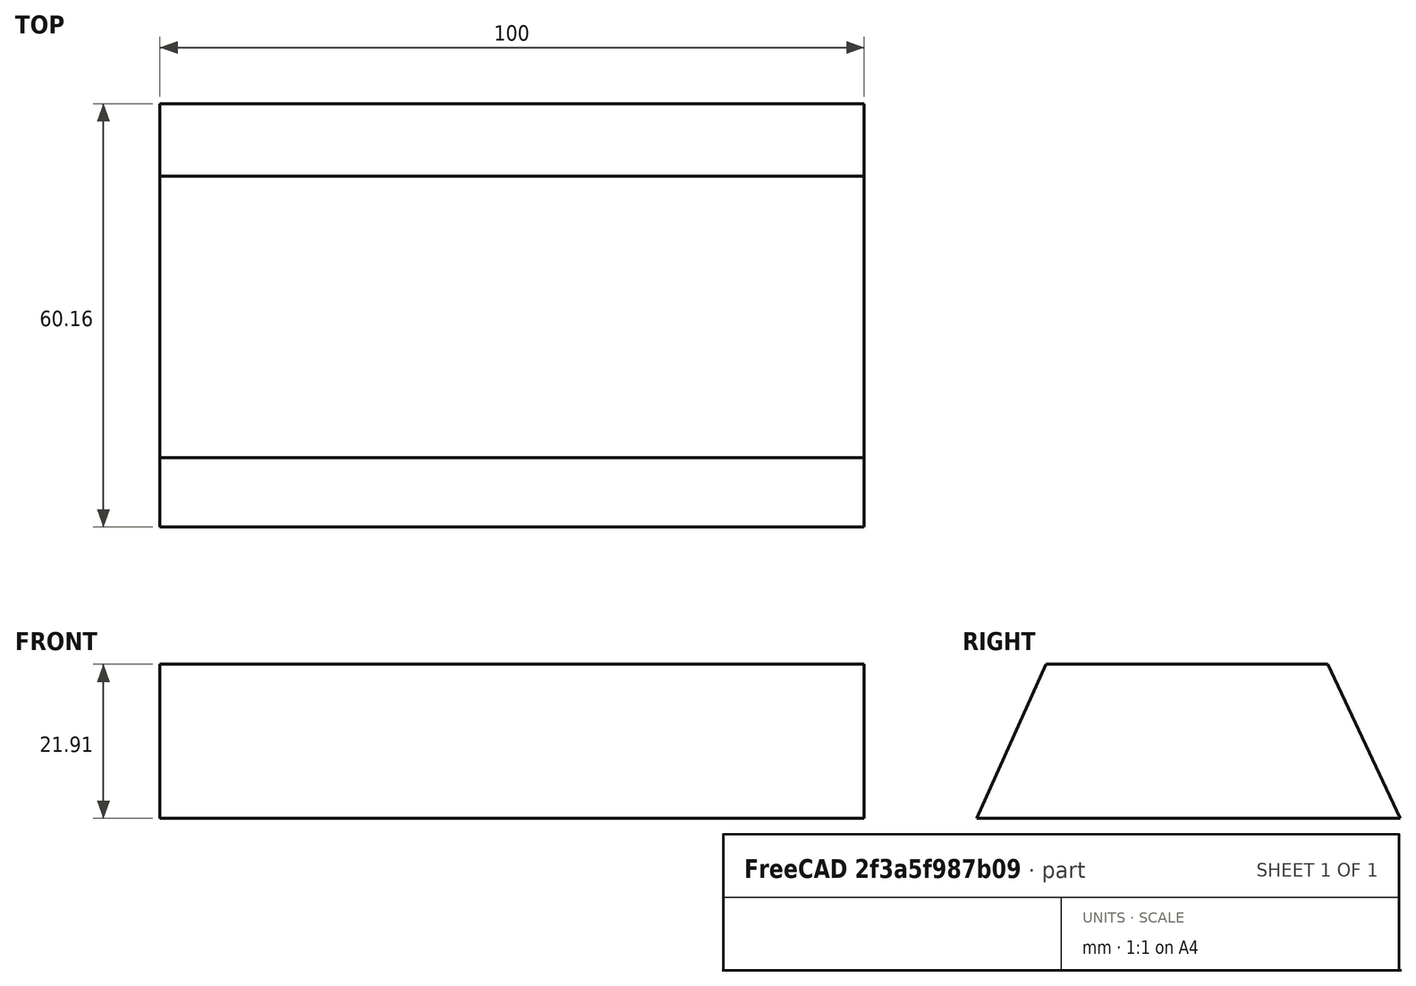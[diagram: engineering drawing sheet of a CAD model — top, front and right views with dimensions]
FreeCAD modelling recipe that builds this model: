
FCSTD DOCUMENT  (FreeCAD 1.0R39319 (Git))
Label: ojt1_t16r01_gold_bar
License: All rights reserved
LicenseURL: https://en.wikipedia.org/wiki/All_rights_reserved
objects: Sketcher::SketchObject×1, PartDesign::Pad×1, PartDesign::Body×1
note: 6 computed .brp shape members not serialized (recipe doc carries the construction recipe); baked Part::Feature solids carry a one-line shape summary decoded from their .brp

FEATURE [Sketcher::SketchObject] Sketch
  ArcFitTolerance = 1e-06
  AttachmentSupport = -> [YZ_Plane]
  FullyConstrained = false
  MakeInternals = false
  MapMode = 5
  Placement = pos=(0,0,0) rot=(0.57735,0.57735,0.57735;2.0944rad)
  sketch-geometry (4):
    g0: LineSegment StartX=-20.0689 StartY=19.951 StartZ=0 EndX=19.8925 EndY=19.951 EndZ=0
    g1: LineSegment StartX=19.8925 StartY=19.951 StartZ=0 EndX=30.2051 EndY=-1.96334 EndZ=0
    g2: LineSegment StartX=30.2051 StartY=-1.96334 StartZ=0 EndX=-29.9518 EndY=-1.96334 EndZ=0
    g3: LineSegment StartX=-29.9518 StartY=-1.96334 StartZ=0 EndX=-20.0689 EndY=19.951 EndZ=0
  constraints (6):
    c: Horizontal(g0)
    c: Coincident(g0,g1)
    c: Coincident(g1,g2)
    c: Horizontal(g2)
    c: Coincident(g2,g3)
    c: Coincident(g3,g0)
FEATURE [PartDesign::Pad] Pad
  Direction = (1,0,0)
  Length = 100
  Length2 = 10
  Placement = pos=(0,0,0) rot=(1,1,1;2.0944rad)
  Profile = -> Sketch
  ReferenceAxis = -> Sketch [N_Axis]
  Refine = true
  Suppressed = false
  Type = 0
FEATURE [PartDesign::Body] Body
  AllowCompound = false
  Group = -> [Sketch,Pad]
  Origin = -> Origin
  Tip = -> Pad
